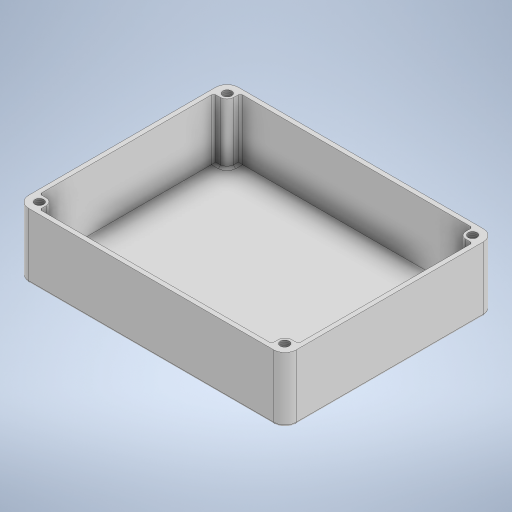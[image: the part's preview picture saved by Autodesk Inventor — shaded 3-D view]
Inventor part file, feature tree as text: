
AUTODESK INVENTOR PART (.ipt)
format: ipt  version: 2024 (Build 280153000, 153)  size: 365,568 bytes
history: native  units: mm
features: fillet x4, other x4, extrude x3, sketch x2, projected_geometry x1
ambient origin geometry x8: Origin, YZ Plane, XZ Plane, XY Plane, X Axis, Y Axis, Z Axis, Center Point
bodies: Solide1 (feature_tree)
feature tree (14):
  sketch  "Esquisse1"
  extrude  "Extrusion1"  Depth=120.0mm
  extrude  "Extrusion2"  Depth=94.0mm
  fillet  "Congé1"  Radius=8.0mm
  fillet  "Congé2"  Radius=8.0mm
  fillet  "Congé3"  Radius=8.0mm
  extrude  "Extrusion3"  Depth=8.0mm
  other  "Filetage1"
  other  "Filetage2"
  other  "Filetage3"
  other  "Filetage4"
  fillet  "Congé4"  Radius=8.0mm
  sketch  "Esquisse2"
  projected_geometry  "Boucle projetée1"
